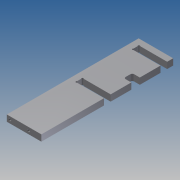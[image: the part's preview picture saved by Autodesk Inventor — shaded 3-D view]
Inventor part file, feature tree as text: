
AUTODESK INVENTOR PART (.ipt)
format: ipt  version: 2012 (Build 160160000, 160)  size: 137,216 bytes
history: native  units: mm
features: reference x6, sketch x3, extrude x2, hole x1
ambient origin geometry x8: Origin, YZ Plane, XZ Plane, XY Plane, X Axis, Y Axis, Z Axis, Center Point
bodies: Volumenkörper1 (feature_tree)
feature tree (12):
  extrude  "Extrusion1"  Depth=55.0mm
  extrude  "Extrusion2"  Depth=0.3mm
  hole  "Bohrung1"  [1 undecoded]
  sketch  "Skizze1"  dims[d0=210.0mm d1=55.0mm]
  sketch  "Skizze2"  dims[d2=10.0mm d3=0.0mm d4=0.3mm]
  reference  "Referenz1"
  reference  "Referenz2"
  reference  "Referenz3"
  reference  "Referenz4"
  reference  "Referenz5"
  reference  "Referenz6"
  sketch  "Skizze3"  dims[d5=0.3mm d6=3.0mm d7=3.0mm d8=0.8mm d9=0.8mm d10=0.8mm d11=0.8mm d13=10.6mm d14=45.0mm d15=0.3mm d16=0.3mm d17=12.1mm d18=3.0mm d19=10.0mm d20=0.0mm d21=30.0mm d22=5.0mm d23=5.0mm d24=5.0mm d25=4.134mm d26=12.0mm d27=4.0mm d28=2.0mm d29=90.0deg d30=15.0mm d31=20.594885mm]
note: 1 required parameter value undecoded (feature->parameter linkage not recoverable at this tier; creation-order binding heuristic only, values carry confidence <= 0.55)
